# Revit family: LC1502
name_source: partatom
category: Luminarias
units: mm (PartAtom-declared; Revit-internal decimal feet)

## family parameters
Compartido = No
Corte con vacíos al cargar = No
Cota de conector redondo = Diámetro de uso
Origen de luz = No
Punto de cálculo de habitación = No
Se basa en plano de trabajo = Sí
Siempre vertical = No
Tipo de pieza = Normal

## types (1)
- LC1502
    Altura = 24 mm  [stored 0.0787402 ft]
    Ancho = 20 mm  [stored 0.0656168 ft]
    Comentarios de vataje = 24V
    Costo = 0 $
    Descripción = PERFIL DE ALUMINIO ARMADO DE 1M DE TIRA LED 2835 CON UNA POTENCIA DE 10W DE 1000MM DE LARGO POR 20MM DE ANCHO POR 24MM DE ALTO, INSTALACION EMPOTRADO EN SUPERFICIE CON 0.2M DE CABLE. PESO MAXIMO PARA SOPORTAR 24.2kN. PRESENTACION DE 1 METRO. IP 67, TEMPERATURA DE COLOR A BLANCO CALIDO 3000K, ALIMENTADO A 24V.
    Elevación por defecto = 0 mm  [stored 0 ft]
    Fabricante = BRILLANT
    Lámpara = 2835 SMD
    Modelo = LC1502

note: [stored X ft] marks values corroborated as IEEE doubles in the binary element streams (Revit-internal decimal feet)

## geometry (parser evidence)
native form markers: Blend x2
no freeform markers — native parametric forms only
